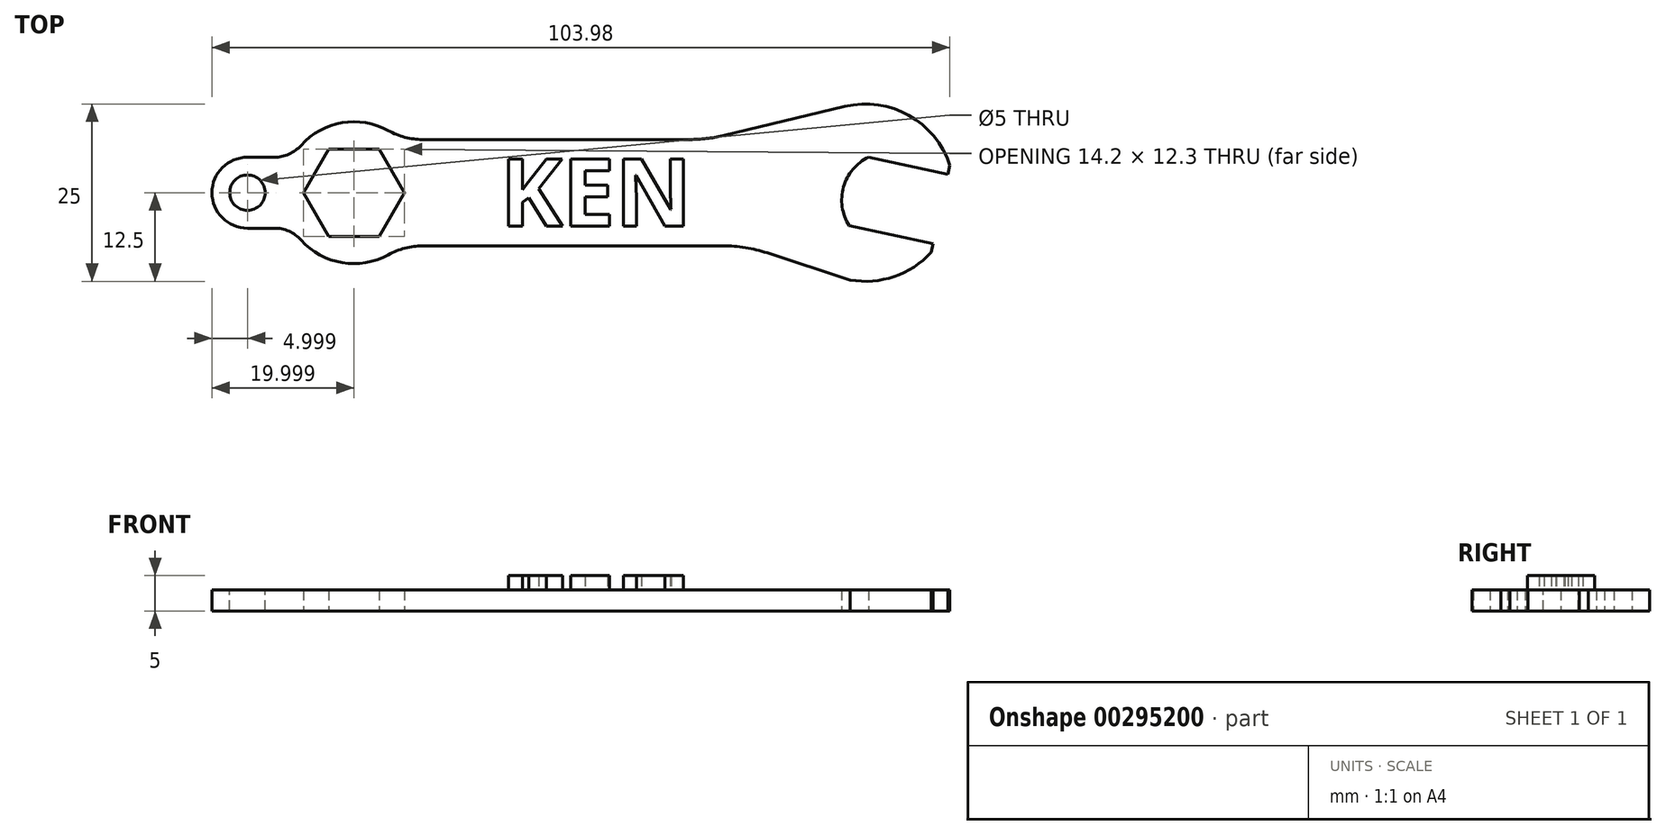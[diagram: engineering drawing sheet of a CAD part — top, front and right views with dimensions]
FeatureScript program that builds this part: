
annotation { "Feature Type Name" : "Feature", "Feature Type Description" : "" }
export const myFeature = defineFeature(function(context is Context, id is Id, definition is map)
    precondition{}
    {
        {
            var Q0;
            Q0=qCreatedBy(makeId("Top.planeOp"),FACE);
            var sketch = newSketch(context, id + "F0", { "sketchPlane" : qUnion([Q0])});
            skLineSegment(sketch, "E0.bottom", {"start": v(7.98, 7.5) * mm, "end": v(-29.67, 7.5) * mm});
            skLineSegment(sketch, "E0.top", {"start": v(12.67, -7.5) * mm, "end": v(-29.67, -7.5) * mm});
            skPoint(sketch, "E0.middle", {"position": v(0, 0) * mm});
            skArc(sketch, "E1", {"start": v(-34.5, 8.75) * mm, "mid": v(-41.02, 9.86) * mm, "end": v(-46.8, 6.67) * mm});
            skPoint(sketch, "E1.centerSnap0", {"position": v(-32.74, 0) * mm});
            skPoint(sketch, "E2.visualSharp", {"position": v(-32.74, 7.5) * mm});
            skArc(sketch, "E2.filletArc", {"start": v(-34.5, 8.75) * mm, "mid": v(-32.17, 7.82) * mm, "end": v(-29.67, 7.5) * mm});
            skPoint(sketch, "E3.visualSharp", {"position": v(-32.74, -7.5) * mm});
            skArc(sketch, "E3.filletArc", {"start": v(-29.67, -7.5) * mm, "mid": v(-32.17, -7.82) * mm, "end": v(-34.5, -8.75) * mm});
            skCircle(sketch, "E4.cCircle", {"center": v(-39.35, 0) * mm, "radius": 6.15 * mm, "construction": true});
            skLineSegment(sketch, "E4.0", {"start": v(-42.9, 6.15) * mm, "end": v(-35.8, 6.15) * mm});
            skLineSegment(sketch, "E4.1", {"start": v(-35.8, 6.15) * mm, "end": v(-32.25, 0) * mm});
            skLineSegment(sketch, "E4.2", {"start": v(-32.25, 0) * mm, "end": v(-35.8, -6.15) * mm});
            skLineSegment(sketch, "E4.3", {"start": v(-35.8, -6.15) * mm, "end": v(-42.9, -6.15) * mm});
            skLineSegment(sketch, "E4.4", {"start": v(-42.9, -6.15) * mm, "end": v(-46.45, 0) * mm});
            skLineSegment(sketch, "E4.5", {"start": v(-46.45, 0) * mm, "end": v(-42.9, 6.15) * mm});
            skPoint(sketch, "E4.0.midPoint", {"position": v(-39.35, 6.15) * mm});
            skArc(sketch, "E5", {"start": v(30.58, -12.31) * mm, "mid": v(36.78, -11.83) * mm, "end": v(41.98, -8.42) * mm});
            skLineSegment(sketch, "E6", {"start": v(12.63, 8.05) * mm, "end": v(29.83, 12.16) * mm});
            skLineSegment(sketch, "E7", {"start": v(30.58, -12.31) * mm, "end": v(18.88, -8.49) * mm});
            skArc(sketch, "E8.trimOffspring", {"start": v(44.63, 3.85) * mm, "mid": v(38.85, 10.9) * mm, "end": v(29.83, 12.16) * mm});
            skPoint(sketch, "E9.orphan", {"position": v(32.74, -7.5) * mm});
            skPoint(sketch, "E10.orphan", {"position": v(32.74, 7.5) * mm});
            skLineSegment(sketch, "E11", {"start": v(44.36, 2.6) * mm, "end": v(33.16, 5.01) * mm});
            skLineSegment(sketch, "E12.0", {"start": v(42.24, -7.18) * mm, "end": v(30.42, -4.63) * mm});
            skArc(sketch, "E13", {"start": v(33.16, 5.01) * mm, "mid": v(29.64, 0.8) * mm, "end": v(30.42, -4.63) * mm});
            skLineSegment(sketch, "E14.0", {"start": v(44.63, 3.85) * mm, "end": v(44.36, 2.6) * mm});
            skLineSegment(sketch, "E15.trimOffspring", {"start": v(42.24, -7.18) * mm, "end": v(41.98, -8.42) * mm});
            skLineSegment(sketch, "E16.bottom", {"start": v(-54.35, 5) * mm, "end": v(-50.53, 5) * mm});
            skLineSegment(sketch, "E16.top", {"start": v(-54.35, -5) * mm, "end": v(-50.53, -5) * mm});
            skLineSegment(sketch, "E16.left", {"start": v(-59.35, 0) * mm, "end": v(-59.35, 0) * mm});
            skPoint(sketch, "E16.middle", {"position": v(-49.35, 0) * mm});
            skPoint(sketch, "E17.orphan", {"position": v(-39.35, 5) * mm});
            skLineSegment(sketch, "E18.trimOffspring", {"start": v(-43.57, 5) * mm, "end": v(-42.93, 5) * mm});
            skLineSegment(sketch, "E19.trimOffspring", {"start": v(-43.57, -5) * mm, "end": v(-42.93, -5) * mm});
            skPoint(sketch, "E20.orphan", {"position": v(-39.35, -5) * mm});
            skArc(sketch, "E21.trimOffspring", {"start": v(-46.8, -6.67) * mm, "mid": v(-41.02, -9.86) * mm, "end": v(-34.5, -8.75) * mm});
            skPoint(sketch, "E22.visualSharp", {"position": v(-48.01, 5) * mm});
            skArc(sketch, "E22.filletArc", {"start": v(-50.53, 5) * mm, "mid": v(-48.49, 5.44) * mm, "end": v(-46.8, 6.67) * mm});
            skPoint(sketch, "E23.visualSharp", {"position": v(-48.01, -5) * mm});
            skArc(sketch, "E23.filletArc", {"start": v(-46.8, -6.67) * mm, "mid": v(-48.49, -5.44) * mm, "end": v(-50.53, -5) * mm});
            skPoint(sketch, "E24.visualSharp", {"position": v(-59.35, 5) * mm});
            skArc(sketch, "E24.filletArc", {"start": v(-54.35, 5) * mm, "mid": v(-57.89, 3.54) * mm, "end": v(-59.35, 0) * mm});
            skPoint(sketch, "E25.visualSharp", {"position": v(-59.35, -5) * mm});
            skArc(sketch, "E25.filletArc", {"start": v(-59.35, 0) * mm, "mid": v(-57.89, -3.54) * mm, "end": v(-54.35, -5) * mm});
            skPoint(sketch, "E26.visualSharp", {"position": v(10.34, 7.5) * mm});
            skArc(sketch, "E26.filletArc", {"start": v(7.98, 7.5) * mm, "mid": v(10.32, 7.64) * mm, "end": v(12.63, 8.05) * mm});
            skPoint(sketch, "E27.visualSharp", {"position": v(15.85, -7.5) * mm});
            skArc(sketch, "E27.filletArc", {"start": v(18.88, -8.49) * mm, "mid": v(15.81, -7.75) * mm, "end": v(12.67, -7.5) * mm});
            skSolve(sketch);
        }
        {
            var Q0;
            Q0=makeQuery(id+"F0.imprint","IMPRINT",FACE,{"disambiguationData":[TD([[makeQuery(id+"F0.imprint","IMPRINT",EDGE,{"derivedFrom":sQuery(id+"F0.wireOp",EDGE,"E0.bottom")}),1.0]])]});
            extrude(context, id + "F1", {"entities" : qUnion([Q0]), "depth" : 3 * mm});
        }
        {
            var Q0;
            Q0=makeQuery(id+"F1.opExtrude","CAP_FACE",FACE,{"disambiguationData":[OSD([sQuery(id+"F0.wireOp",EDGE,"E0.bottom"),sQuery(id+"F0.wireOp",EDGE,"E0.top"),sQuery(id+"F0.wireOp",EDGE,"E1"),sQuery(id+"F0.wireOp",EDGE,"E2.filletArc"),sQuery(id+"F0.wireOp",EDGE,"E3.filletArc"),sQuery(id+"F0.wireOp",EDGE,"E4.0"),sQuery(id+"F0.wireOp",EDGE,"E4.1"),sQuery(id+"F0.wireOp",EDGE,"E4.2"),sQuery(id+"F0.wireOp",EDGE,"E4.3"),sQuery(id+"F0.wireOp",EDGE,"E4.4"),sQuery(id+"F0.wireOp",EDGE,"E4.5"),sQuery(id+"F0.wireOp",EDGE,"E5"),sQuery(id+"F0.wireOp",EDGE,"E6"),sQuery(id+"F0.wireOp",EDGE,"E7"),sQuery(id+"F0.wireOp",EDGE,"E8.trimOffspring"),sQuery(id+"F0.wireOp",EDGE,"E11"),sQuery(id+"F0.wireOp",EDGE,"E12.0"),sQuery(id+"F0.wireOp",EDGE,"E13"),sQuery(id+"F0.wireOp",EDGE,"E14.0"),sQuery(id+"F0.wireOp",EDGE,"E15.trimOffspring"),sQuery(id+"F0.wireOp",EDGE,"E16.bottom"),sQuery(id+"F0.wireOp",EDGE,"E16.top"),sQuery(id+"F0.wireOp",EDGE,"E21.trimOffspring"),sQuery(id+"F0.wireOp",EDGE,"E22.filletArc"),sQuery(id+"F0.wireOp",EDGE,"E23.filletArc"),sQuery(id+"F0.wireOp",EDGE,"E24.filletArc"),sQuery(id+"F0.wireOp",EDGE,"E25.filletArc"),sQuery(id+"F0.wireOp",EDGE,"E26.filletArc"),sQuery(id+"F0.wireOp",EDGE,"E27.filletArc")])],"isStart":false});
            var sketch = newSketch(context, id + "F2", { "sketchPlane" : qUnion([Q0])});
            skText(sketch, "E28", { "text": "KEN", "fontName": "OpenSans-Bold.ttf"});
            const initialGuessF2  = {"E28": [-0.01878, -0.00471, 1, 0, 0.00955]};
            skSetInitialGuess(sketch, initialGuessF2);
            skSolve(sketch);
        }
        {
            var Q0;
            Q0=makeQuery(id+"F2.imprint","IMPRINT",FACE,{"disambiguationData":[TD([[makeQuery(id+"F2.imprint","IMPRINT",EDGE,{"derivedFrom":sQuery(id+"F2.wireOp",EDGE,"E28.sketch_text.stroke-0")}),-1.0]])]});
            var Q1;
            Q1=makeQuery(id+"F2.imprint","IMPRINT",FACE,{"disambiguationData":[TD([[makeQuery(id+"F2.imprint","IMPRINT",EDGE,{"derivedFrom":sQuery(id+"F2.wireOp",EDGE,"E28.sketch_text.stroke-13")}),-1.0]])]});
            var Q2;
            Q2=makeQuery(id+"F2.imprint","IMPRINT",FACE,{"disambiguationData":[TD([[makeQuery(id+"F2.imprint","IMPRINT",EDGE,{"derivedFrom":sQuery(id+"F2.wireOp",EDGE,"E28.sketch_text.stroke-25")}),-1.0]])]});
            var Q3;
            Q3=makeQuery(id+"F2.imprint","IMPRINT",FACE,{"disambiguationData":[TD([[makeQuery(id+"F2.imprint","IMPRINT",EDGE,{"derivedFrom":sQuery(id+"F2.wireOp",EDGE,"E28.sketch_text.stroke-31")}),-1.0]])]});
            var Q4;
            Q4=makeQuery(id+"F2.imprint","IMPRINT",FACE,{"disambiguationData":[TD([[makeQuery(id+"F2.imprint","IMPRINT",EDGE,{"derivedFrom":sQuery(id+"F2.wireOp",EDGE,"E28.sketch_text.stroke-41")}),-1.0]])]});
            var Q5;
            Q5=makeQuery(id+"F2.imprint","IMPRINT",FACE,{"disambiguationData":[TD([[makeQuery(id+"F2.imprint","IMPRINT",EDGE,{"derivedFrom":sQuery(id+"F2.wireOp",EDGE,"E28.sketch_text.stroke-45")}),-1.0]])]});
            extrude(context, id + "F3", {"entities" : qUnion([Q0, Q1, Q2, Q3, Q4, Q5]), "operationType" : NewBodyOperationType.ADD, "depth" : 2 * mm});
        }
        {
            var Q0;
            Q0=makeQuery(id+"F1.opExtrude","CAP_FACE",FACE,{"disambiguationData":[OSD([sQuery(id+"F0.wireOp",EDGE,"E0.bottom"),sQuery(id+"F0.wireOp",EDGE,"E0.top"),sQuery(id+"F0.wireOp",EDGE,"E1"),sQuery(id+"F0.wireOp",EDGE,"E2.filletArc"),sQuery(id+"F0.wireOp",EDGE,"E3.filletArc"),sQuery(id+"F0.wireOp",EDGE,"E4.0"),sQuery(id+"F0.wireOp",EDGE,"E4.1"),sQuery(id+"F0.wireOp",EDGE,"E4.2"),sQuery(id+"F0.wireOp",EDGE,"E4.3"),sQuery(id+"F0.wireOp",EDGE,"E4.4"),sQuery(id+"F0.wireOp",EDGE,"E4.5"),sQuery(id+"F0.wireOp",EDGE,"E5"),sQuery(id+"F0.wireOp",EDGE,"E6"),sQuery(id+"F0.wireOp",EDGE,"E7"),sQuery(id+"F0.wireOp",EDGE,"E8.trimOffspring"),sQuery(id+"F0.wireOp",EDGE,"E11"),sQuery(id+"F0.wireOp",EDGE,"E12.0"),sQuery(id+"F0.wireOp",EDGE,"E13"),sQuery(id+"F0.wireOp",EDGE,"E14.0"),sQuery(id+"F0.wireOp",EDGE,"E15.trimOffspring"),sQuery(id+"F0.wireOp",EDGE,"E16.bottom"),sQuery(id+"F0.wireOp",EDGE,"E16.top"),sQuery(id+"F0.wireOp",EDGE,"E21.trimOffspring"),sQuery(id+"F0.wireOp",EDGE,"E22.filletArc"),sQuery(id+"F0.wireOp",EDGE,"E23.filletArc"),sQuery(id+"F0.wireOp",EDGE,"E24.filletArc"),sQuery(id+"F0.wireOp",EDGE,"E25.filletArc"),sQuery(id+"F0.wireOp",EDGE,"E26.filletArc"),sQuery(id+"F0.wireOp",EDGE,"E27.filletArc")])],"isStart":false});
            var sketch = newSketch(context, id + "F4", { "sketchPlane" : qUnion([Q0])});
            skCircle(sketch, "E29", {"center": v(-54.35, 0) * mm, "radius": 2.5 * mm});
            skSolve(sketch);
        }
        {
            var Q0;
            Q0=makeQuery(id+"F4.imprint","IMPRINT",FACE,{"disambiguationData":[TD([[makeQuery(id+"F4.imprint","IMPRINT",EDGE,{"derivedFrom":sQuery(id+"F4.wireOp",EDGE,"E29")}),1.0]])]});
            var Q1;
            Q1=makeQuery(id+"F1.opExtrude","CAP_FACE",FACE,{"disambiguationData":[OSD([sQuery(id+"F0.wireOp",EDGE,"E0.bottom"),sQuery(id+"F0.wireOp",EDGE,"E0.top"),sQuery(id+"F0.wireOp",EDGE,"E1"),sQuery(id+"F0.wireOp",EDGE,"E2.filletArc"),sQuery(id+"F0.wireOp",EDGE,"E3.filletArc"),sQuery(id+"F0.wireOp",EDGE,"E4.0"),sQuery(id+"F0.wireOp",EDGE,"E4.1"),sQuery(id+"F0.wireOp",EDGE,"E4.2"),sQuery(id+"F0.wireOp",EDGE,"E4.3"),sQuery(id+"F0.wireOp",EDGE,"E4.4"),sQuery(id+"F0.wireOp",EDGE,"E4.5"),sQuery(id+"F0.wireOp",EDGE,"E5"),sQuery(id+"F0.wireOp",EDGE,"E6"),sQuery(id+"F0.wireOp",EDGE,"E7"),sQuery(id+"F0.wireOp",EDGE,"E8.trimOffspring"),sQuery(id+"F0.wireOp",EDGE,"E11"),sQuery(id+"F0.wireOp",EDGE,"E12.0"),sQuery(id+"F0.wireOp",EDGE,"E13"),sQuery(id+"F0.wireOp",EDGE,"E14.0"),sQuery(id+"F0.wireOp",EDGE,"E15.trimOffspring"),sQuery(id+"F0.wireOp",EDGE,"E16.bottom"),sQuery(id+"F0.wireOp",EDGE,"E16.top"),sQuery(id+"F0.wireOp",EDGE,"E21.trimOffspring"),sQuery(id+"F0.wireOp",EDGE,"E22.filletArc"),sQuery(id+"F0.wireOp",EDGE,"E23.filletArc"),sQuery(id+"F0.wireOp",EDGE,"E24.filletArc"),sQuery(id+"F0.wireOp",EDGE,"E25.filletArc"),sQuery(id+"F0.wireOp",EDGE,"E26.filletArc"),sQuery(id+"F0.wireOp",EDGE,"E27.filletArc")])],"isStart":true});
            extrude(context, id + "F5", {"entities" : qUnion([Q0]), "operationType" : NewBodyOperationType.REMOVE, "endBound" : BoundingType.UP_TO_SURFACE, "oppositeDirection" : true, "endBoundEntityFace" : qUnion([Q1]), "depth" : 25 * mm});
        }
    });
